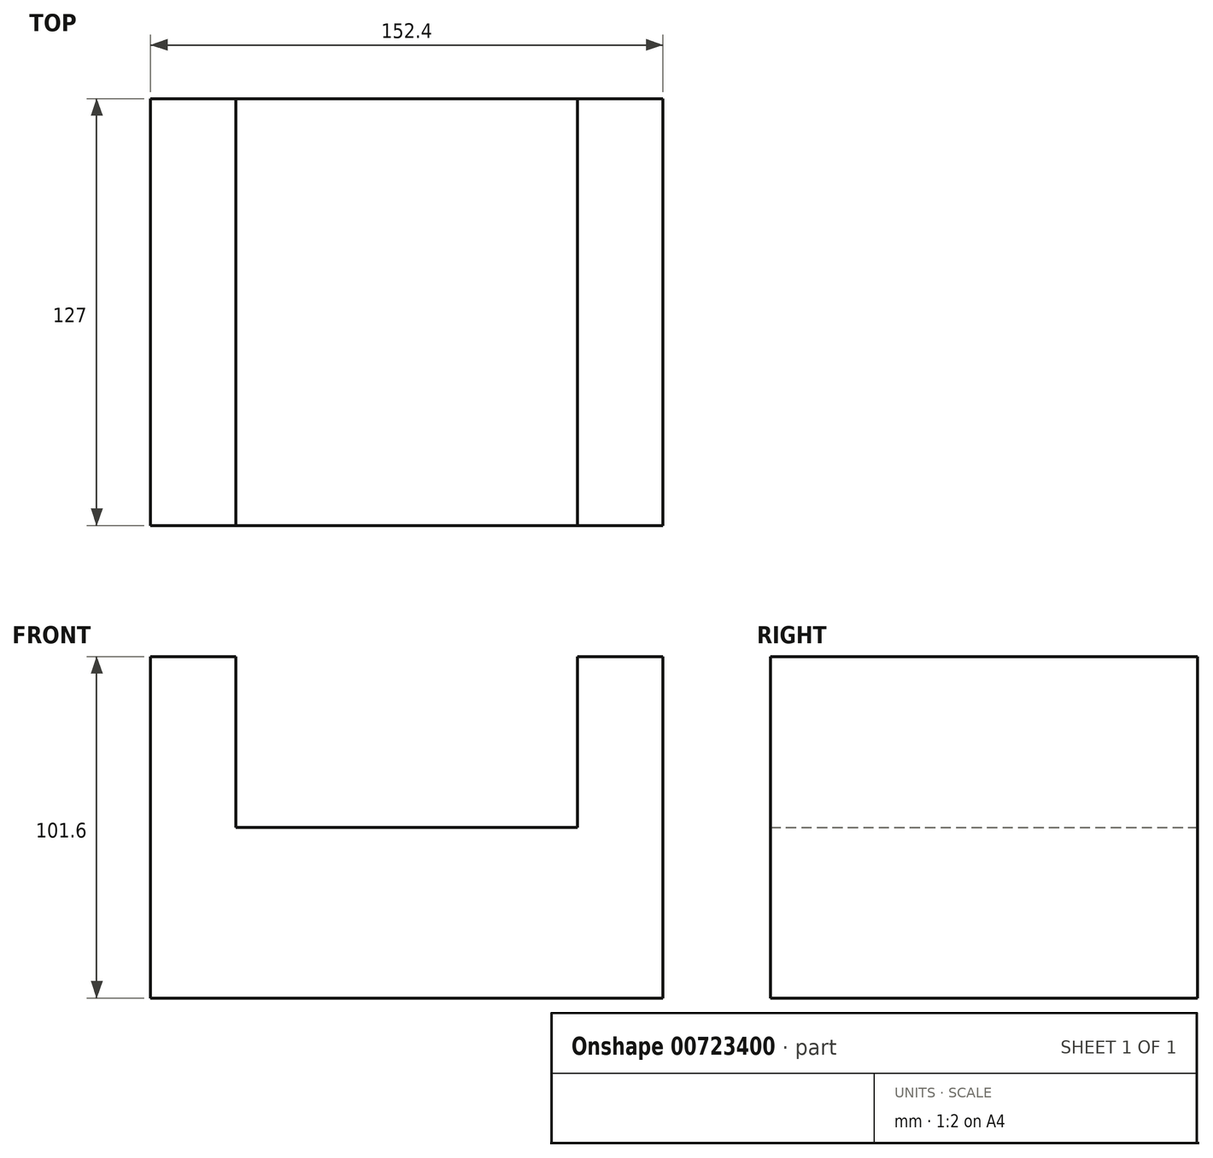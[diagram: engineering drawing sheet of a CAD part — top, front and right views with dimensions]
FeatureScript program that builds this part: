
annotation { "Feature Type Name" : "Feature", "Feature Type Description" : "" }
export const myFeature = defineFeature(function(context is Context, id is Id, definition is map)
    precondition{}
    {
        {
            var Q0;
            Q0=qCreatedBy(makeId("Front.planeOp"),FACE);
            var sketch = newSketch(context, id + "F0", { "sketchPlane" : qUnion([Q0])});
            skLineSegment(sketch, "E0", {"start": v(-75.78, -75.2) * mm, "end": v(76.62, -75.2) * mm});
            skLineSegment(sketch, "E1", {"start": v(76.62, -75.2) * mm, "end": v(76.62, 26.4) * mm});
            skLineSegment(sketch, "E2", {"start": v(76.62, 26.4) * mm, "end": v(51.22, 26.4) * mm});
            skLineSegment(sketch, "E3", {"start": v(51.22, 26.4) * mm, "end": v(51.22, -24.4) * mm});
            skLineSegment(sketch, "E4", {"start": v(-75.78, -75.2) * mm, "end": v(-75.78, 26.4) * mm});
            skLineSegment(sketch, "E5", {"start": v(-75.78, 26.4) * mm, "end": v(-50.38, 26.4) * mm});
            skLineSegment(sketch, "E6", {"start": v(-50.38, 26.4) * mm, "end": v(-50.38, -24.4) * mm});
            skLineSegment(sketch, "E7", {"start": v(-50.38, -24.4) * mm, "end": v(51.22, -24.4) * mm});
            skSolve(sketch);
        }
        {
            var Q0;
            Q0 = qSketchRegion(id + "F0", true);
            extrude(context, id + "F1", {"entities" : qUnion([Q0]), "depth" : 127 * mm, "offsetDistance" : 25.4 * mm});
        }
    });
